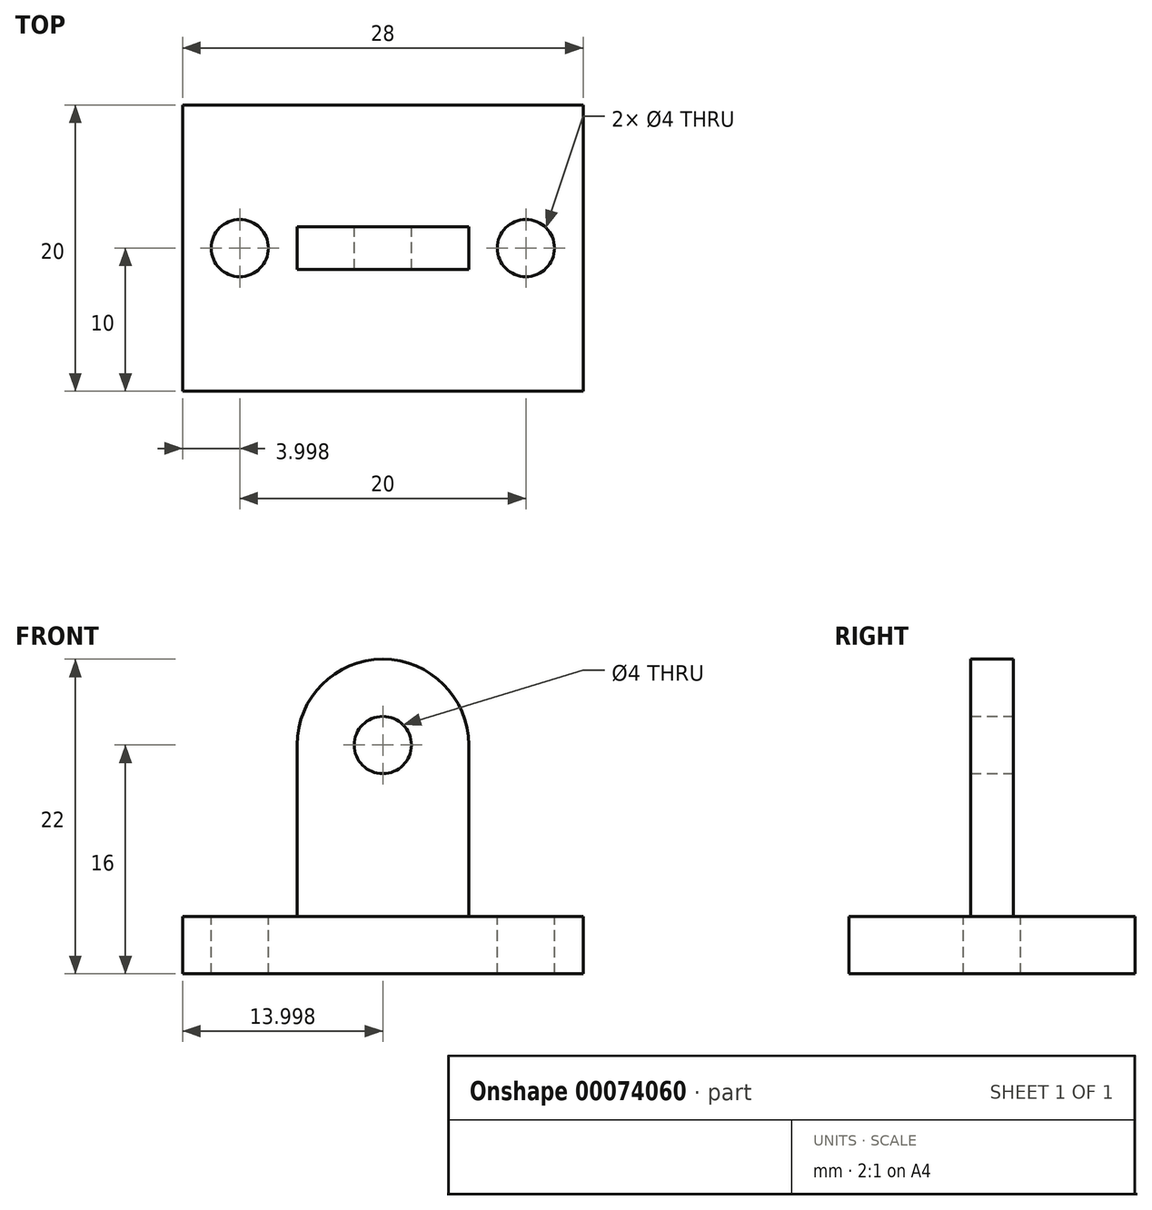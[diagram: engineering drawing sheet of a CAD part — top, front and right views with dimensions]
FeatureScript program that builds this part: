
annotation { "Feature Type Name" : "Feature", "Feature Type Description" : "" }
export const myFeature = defineFeature(function(context is Context, id is Id, definition is map)
    precondition{}
    {
        {
            var Q0;
            Q0=qCreatedBy(makeId("Front.planeOp"),FACE);
            var sketch = newSketch(context, id + "F0", { "sketchPlane" : qUnion([Q0])});
            skPoint(sketch, "E0.rect.middle", {"position": v(0, 0) * mm});
            skLineSegment(sketch, "E1.bottom", {"start": v(17.33, 0) * mm, "end": v(5.33, 0) * mm});
            skLineSegment(sketch, "E1.top", {"start": v(17.33, 12) * mm, "end": v(5.33, 12) * mm});
            skLineSegment(sketch, "E1.left", {"start": v(17.33, 0) * mm, "end": v(17.33, 12) * mm});
            skLineSegment(sketch, "E1.right", {"start": v(5.33, 0) * mm, "end": v(5.33, 12) * mm});
            skCircle(sketch, "E2", {"center": v(11.33, 12) * mm, "radius": 6 * mm});
            skCircle(sketch, "E3", {"center": v(11.33, 12) * mm, "radius": 2 * mm});
            skLineSegment(sketch, "E4", {"start": v(5.33, 0) * mm, "end": v(-2.67, 0) * mm});
            skLineSegment(sketch, "E5", {"start": v(-2.67, 0) * mm, "end": v(-2.67, -4) * mm});
            skLineSegment(sketch, "E6", {"start": v(-2.67, -4) * mm, "end": v(25.33, -4) * mm});
            skLineSegment(sketch, "E7", {"start": v(25.33, -4) * mm, "end": v(25.33, 0) * mm});
            skLineSegment(sketch, "E8", {"start": v(25.33, 0) * mm, "end": v(17.33, 0) * mm});
            skSolve(sketch);
        }
        {
            var Q0;
            Q0=makeQuery(id+"F0.imprint","IMPRINT",FACE,{"disambiguationData":[TD([[makeQuery(id+"F0.imprint","IMPRINT",EDGE,{"derivedFrom":sQuery(id+"F0.wireOp",EDGE,"E1.bottom")}),1.0]])]});
            extrude(context, id + "F1", {"entities" : qUnion([Q0]), "depth" : 10 * mm, "hasSecondDirection" : true, "secondDirectionOppositeDirection" : true, "secondDirectionDepth" : 10 * mm});
        }
        {
            var Q0;
            Q0=makeQuery(id+"F0.imprint","IMPRINT",FACE,{"disambiguationData":[TD([[makeQuery(id+"F0.imprint","IMPRINT",EDGE,{"derivedFrom":sQuery(id+"F0.wireOp",EDGE,"E1.bottom")}),-1.0]])]});
            var Q1;
            {var subQ1=sQuery(id+"F0.wireOp",EDGE,"E1.top");var subQ3=sQuery(id+"F0.wireOp",EDGE,"E3");var subQ4=makeQuery(id+"F0.imprint","INTERSECT",VERTEX,{"disambiguationData":[OD(0.0)],"derivedFrom":[subQ1,subQ3]});Q1=makeQuery(id+"F0.imprint","IMPRINT",FACE,{"disambiguationData":[TD([[makeQuery(id+"F0.imprint","IMPRINT",EDGE,{"disambiguationData":[TD([[subQ4,-1.0]])],"derivedFrom":subQ3}),-1.0]])]});}
            var Q2;
            {var subQ1=sQuery(id+"F0.wireOp",EDGE,"E1.top");var subQ3=sQuery(id+"F0.wireOp",EDGE,"E3");var subQ4=makeQuery(id+"F0.imprint","INTERSECT",VERTEX,{"disambiguationData":[OD(0.0)],"derivedFrom":[subQ1,subQ3]});Q2=makeQuery(id+"F0.imprint","IMPRINT",FACE,{"disambiguationData":[TD([[makeQuery(id+"F0.imprint","IMPRINT",EDGE,{"disambiguationData":[TD([[subQ4,1.0]])],"derivedFrom":subQ3}),-1.0]])]});}
            extrude(context, id + "F2", {"entities" : qUnion([Q0, Q1, Q2]), "operationType" : NewBodyOperationType.ADD, "depth" : 1.5 * mm, "hasSecondDirection" : true, "secondDirectionOppositeDirection" : true, "secondDirectionDepth" : 1.5 * mm});
        }
        {
            var Q0;
            Q0=makeQuery(id+"F1.opExtrude","SWEPT_FACE",FACE,{"disambiguationData":[OSD([sQuery(id+"F0.wireOp",EDGE,"E1.bottom"),sQuery(id+"F0.wireOp",EDGE,"E4"),sQuery(id+"F0.wireOp",EDGE,"E8")])]});
            var sketch = newSketch(context, id + "F3", { "sketchPlane" : qUnion([Q0])});
            skCircle(sketch, "E9", {"center": v(1.33, 0) * mm, "radius": 2 * mm});
            skLineSegment(sketch, "E10.bottom", {"start": v(-2.67, 10) * mm, "end": v(5.33, 10) * mm, "construction": true});
            skLineSegment(sketch, "E10.top", {"start": v(-2.67, -10) * mm, "end": v(5.33, -10) * mm, "construction": true});
            skLineSegment(sketch, "E10.left", {"start": v(-2.67, 10) * mm, "end": v(-2.67, -10) * mm, "construction": true});
            skLineSegment(sketch, "E10.right", {"start": v(5.33, 10) * mm, "end": v(5.33, -10) * mm, "construction": true});
            skLineSegment(sketch, "E11", {"start": v(-2.67, 10) * mm, "end": v(5.33, -10) * mm, "construction": true});
            skLineSegment(sketch, "E12", {"start": v(5.33, 10) * mm, "end": v(-2.67, -10) * mm, "construction": true});
            skLineSegment(sketch, "E13", {"start": v(11.33, 10) * mm, "end": v(11.33, -10) * mm, "construction": true});
            skCircle(sketch, "E14.MirrorC", {"center": v(21.33, 0) * mm, "radius": 2 * mm});
            skSolve(sketch);
        }
        {
            var Q0;
            Q0 = qSketchRegion(id + "F3", true);
            extrude(context, id + "F4", {"entities" : qUnion([Q0]), "operationType" : NewBodyOperationType.REMOVE, "oppositeDirection" : true, "depth" : 5 * mm, "hasSecondDirection" : true, "secondDirectionOppositeDirection" : false, "secondDirectionDepth" : 5 * mm});
        }
    });
